# Revit family: Chair-Multi_Purpose-Allermuir-Soul-A784
name_source: partatom
category: Furniture
revit_build: Autodesk Revit MEP 2012 (Build: 20110309_2315)
units: mm (PartAtom-declared; Revit-internal decimal feet)

## types (1)
- A784
    04 CSI = 12 51 00
    95 CSI = 12510
    Arm = Fabric - Allermuir - Smooth - Black
    Arm Height = 2' - 3"
    Arm Rest = Fabric - Allermuir - Smooth - Black
    Assembly Code = E2020200
    Back = Laminate - Allermuir - White
    Back Rest = Laminate - Allermuir - White
    Base = Metal - Allermuir - Chrome - Polished
    Brochure URL = http://www.allermuir.net
    CAD Blocks URL = http://www.allermuir.net
    Color Availability = See price list for material options
    Cushion = Fabric - Allermuir - Smooth - Black
    Description = Side chair, plastic seat and back, no arms
    Fabric Spec Sheets = http://www.allermuir.net
    LEED Stats URL = http://www.allermuir.net
    Manufacturer = Allermuir
    Manufacturer Fax = (419) 887 5805
    Model = A784
    Overall Depth = 1' - 10"
    Overall Height = 2' - 7"
    Overall Width = 1' - 10 1/2"
    Plastic Arms in Black = No
    Plastic glides = Yes
    Plugin Data URL = http://products.ecoscorecard.com
    Pricing URL = http://www.allermuir.net
    Product Line = Soul
    Product Page URL = http://www.allermuir.net
    Seat = Fabric - Allermuir - Smooth - Black
    Seat Depth = 1' - 5 1/2"
    Seat Height = 1' - 6"
    Seat Width = 1' - 6 1/2"
    Seat or Top = Fabric - Allermuir - Smooth - Black
    Specifications URL = http://www.allermuir.net
    Stacks = No
    Stand = Metal - Allermuir - Chrome - Polished
    Subcategory = Multi-Purpose Line
    Tubular Steel Legs = Yes
    URL = http://www.allermuir.net
    Weight = 18.0 lb
    ecoScorecard Product Page = http://products.ecoscorecard.com
    ecoScorecard_data = http://thesenatorgroup.ecoscorecard.com

## geometry (parser evidence)
native form markers: Sweep x2
no freeform markers — native parametric forms only
